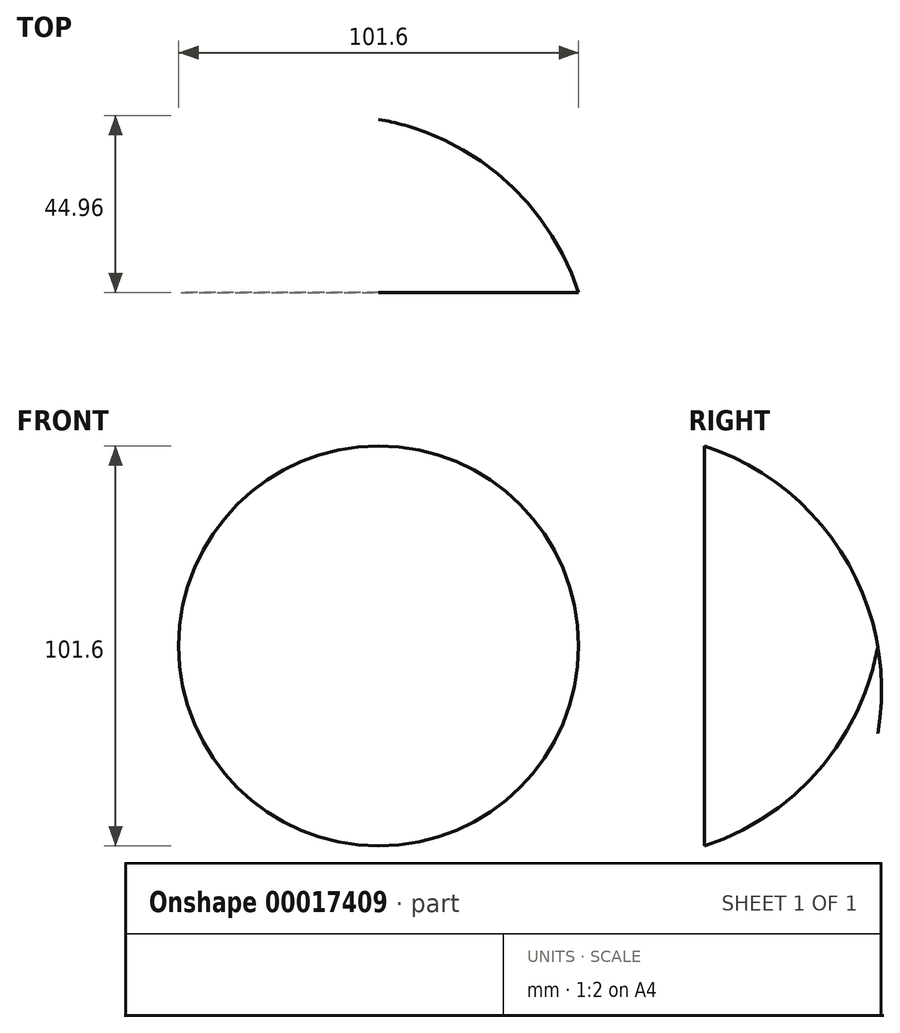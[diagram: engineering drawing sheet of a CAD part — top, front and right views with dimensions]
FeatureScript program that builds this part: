
annotation { "Feature Type Name" : "Feature", "Feature Type Description" : "" }
export const myFeature = defineFeature(function(context is Context, id is Id, definition is map)
    precondition{}
    {
        {
            var Q0;
            Q0=qCreatedBy(makeId("Top.planeOp"),FACE);
            var sketch = newSketch(context, id + "F0", { "sketchPlane" : qUnion([Q0])});
            skLineSegment(sketch, "E0", {"start": v(0, 0) * mm, "end": v(0, 31) * mm});
            skLineSegment(sketch, "E1", {"start": v(0, 0) * mm, "end": v(50.8, 0) * mm});
            skLineSegment(sketch, "E2", {"start": v(0, 31) * mm, "end": v(0, 44) * mm});
            skArc(sketch, "E3", {"start": v(50.8, 0) * mm, "mid": v(31.52, 29.06) * mm, "end": v(0, 44) * mm});
            skSolve(sketch);
        }
        {
            var Q0;
            Q0=makeQuery(id+"F0.imprint","IMPRINT",FACE,{"disambiguationData":[TD([[makeQuery(id+"F0.imprint","IMPRINT",EDGE,{"derivedFrom":sQuery(id+"F0.wireOp",EDGE,"E0")}),-1.0]])]});
            var Q1;
            Q1=sQuery(id+"F0.wireOp",EDGE,"E0");
            revolve(context, id + "F1", {"entities" : qUnion([Q0]), "axis" : qUnion([Q1]), "revolveType" : RevolveType.ONE_DIRECTION, "angle" : 360 * degree});
        }
    });
